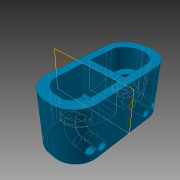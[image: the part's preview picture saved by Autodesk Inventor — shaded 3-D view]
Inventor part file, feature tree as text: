
AUTODESK INVENTOR PART (.ipt)
format: ipt  version: 2015 SP2 (Build 190223200, 223)  size: 238,080 bytes
history: native  units: in
note: dims shown in document units (in); Inventor stores cm internally (conversion verified against a paired STEP export)
features: extrude x4, mirror x4, sketch x4, plane x2, fillet x2, revolve x1
ambient origin geometry x8: Origin, YZ Plane, XZ Plane, XY Plane, X Axis, Y Axis, Z Axis, Center Point
bodies: Solid1 (feature_tree)
feature tree (17):
  extrude  "Extrusion1"  TaperAngle=105.0deg  [1 undecoded]
  extrude  "Extrusion2"  Depth=0.28in TaperAngle=0.0deg
  plane  "Work Plane1"
  mirror  "Mirror1"
  plane  "Work Plane2"
  extrude  "Extrusion3"  Depth=0.18in
  mirror  "Mirror2"
  fillet  "Fillet4"  Radius=0.265in
  fillet  "Fillet5"  Radius=0.04in
  revolve  "Revolution1"  Angle=90.0deg
  mirror  "Mirror3"
  extrude  "Extrusion6"  Depth=0.15in
  mirror  "Mirror10"
  sketch  "Sketch2"  dims[d0=0.425in d1=105.0deg]
  sketch  "Sketch3"  dims[d8=0.03in d10=0.28in d11=0.0in]
  sketch  "Sketch4"  dims[d12=0.06in d13=0.0in d14=0.18in d15=0.265in d16=0.04in d17=0.0in]
  sketch  "Sketch6"  dims[d18=0.045in d20=90.0deg d33=0.15in d34=0.3957in d35=0.03in d36=0.07in d41=0.125in d42=0.175in d43=0.045in d44=0.065in d45=1.0in d46=0.0in]
note: 1 required parameter value undecoded (feature->parameter linkage not recoverable at this tier; creation-order binding heuristic only, values carry confidence <= 0.55)
